# Revit family: Bike_Rack-Saris_Parking-Bike_Dock
name_source: partatom
category: Site
revit_build: Autodesk Revit 2014 (Build: 20140709_2115(x64)
units: mm (PartAtom-declared; Revit-internal decimal feet)

## types (6) — shared parameters
Assembly Code = G2040500
Default Elevation = 4' - 0"
Description = Intuitive, easy to use bike parking for 2 bikes
Height = 2' - 8"
LEED Credit = Meets APBP Guidelines
Manufacturer = Saris Parking
Mount Color = Paint - Saris Parking - Powder Coat - Shuttle Black
Number of Parkable Bikes = 2
Product Documentation Link = https://www.sarisparking.com
Product Page URL = https://www.sarisparking.com
URL = https://www.sarisparking.com

## per-type parameters (varying)
| type | Below Grade Mount | Flange Mount | Length | Model | Pipe Radius | Pipe Size | Pole Length | Tube Round | Tube Square | Weight | Width |
| 1.66" Round Below Grade Mount | Yes | No | 2' - 6" | 2112 | 0' - 0 27/32" | 0' - 1 21/32" | 2' - 8 3/4" | Yes | No | 17.00 lb | 0' - 2" |
| 1.66" Round Flange Mount | No | Yes | 2' - 10" | 2113 | 0' - 0 27/32" | 0' - 1 21/32" | 1' - 9 9/16" | Yes | No | 19.00 lb | 0' - 6" |
| 2.38" Round Below Grade Mount | Yes | No | 2' - 6" | 2112 | 0' - 1 3/16" | 0' - 2 3/8" | 2' - 8 3/4" | Yes | No | 31.00 lb | 0' - 2 13/32" |
| 2.38" Round Flange Mount | No | Yes | 2' - 10" | 2113 | 0' - 1 3/16" | 0' - 2 3/8" | 1' - 9 9/16" | Yes | No | 30.00 lb | 0' - 6" |
| 2" Square Below Grade Mount | Yes | No | 2' - 6" | 2112 | 0' - 1" | 0' - 2" | 2' - 8 3/4" | No | Yes | 38.00 lb | 0' - 2 13/32" |
| 2" Square Flange Mount | No | Yes | 2' - 10" | 2113 | 0' - 1" | 0' - 2" | 1' - 9 9/16" | No | Yes | 34.00 lb | 0' - 6" |

## geometry (parser evidence)
native form markers: Sweep x10
no freeform markers — native parametric forms only
